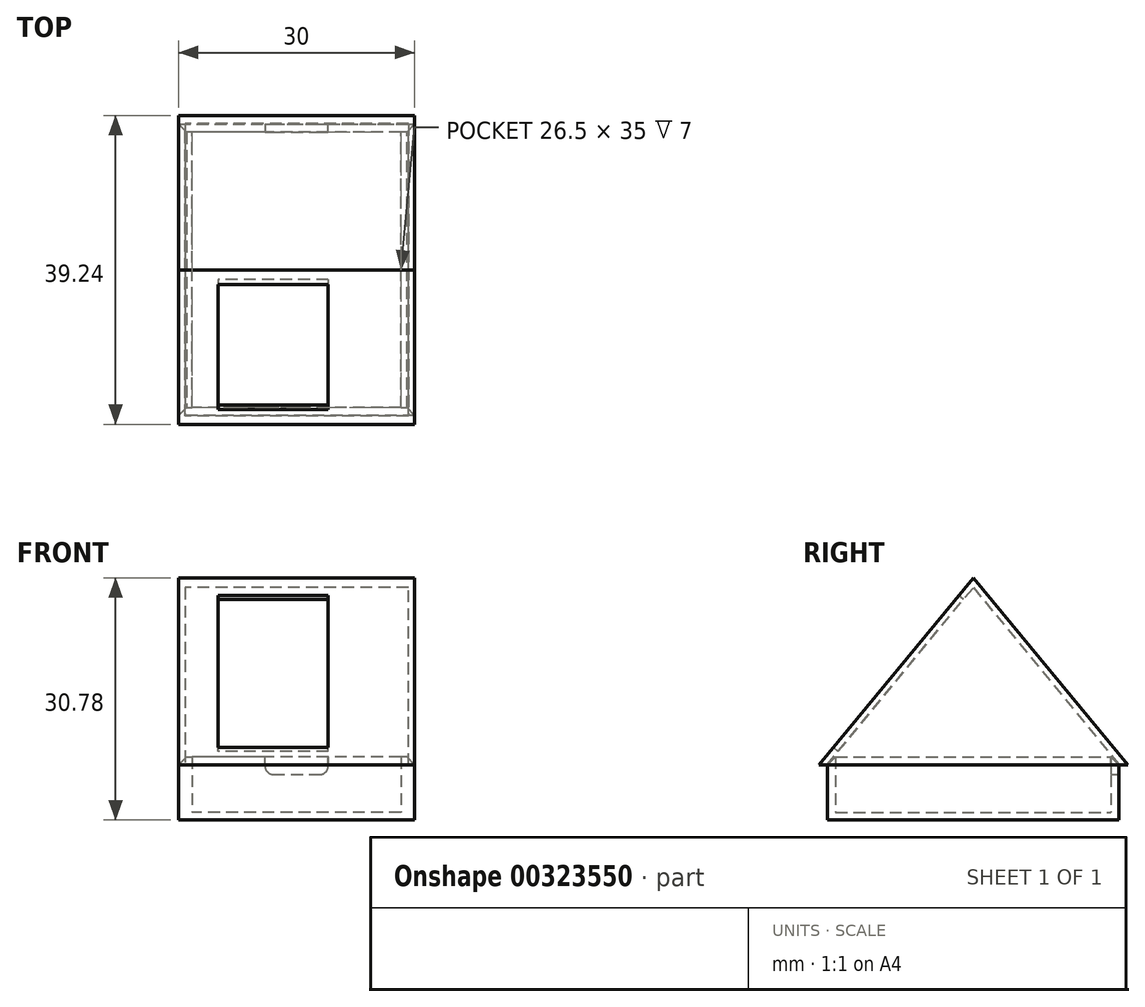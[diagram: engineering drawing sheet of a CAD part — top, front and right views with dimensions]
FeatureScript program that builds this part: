
annotation { "Feature Type Name" : "Feature", "Feature Type Description" : "" }
export const myFeature = defineFeature(function(context is Context, id is Id, definition is map)
    precondition{}
    {
        {
            var Q0;
            Q0=qCreatedBy(makeId("Top.planeOp"),FACE);
            var sketch = newSketch(context, id + "F0", { "sketchPlane" : qUnion([Q0])});
            skLineSegment(sketch, "E0.bottom", {"start": v(13.25, -17.5) * mm, "end": v(-13.25, -17.5) * mm});
            skLineSegment(sketch, "E0.top", {"start": v(13.25, 17.5) * mm, "end": v(-13.25, 17.5) * mm});
            skLineSegment(sketch, "E0.left", {"start": v(13.25, -17.5) * mm, "end": v(13.25, 17.5) * mm});
            skLineSegment(sketch, "E0.right", {"start": v(-13.25, -17.5) * mm, "end": v(-13.25, 17.5) * mm});
            skPoint(sketch, "E0.middle", {"position": v(0, 0) * mm});
            skLineSegment(sketch, "E1.bottom", {"start": v(-15, -18.5) * mm, "end": v(15, -18.5) * mm});
            skLineSegment(sketch, "E1.top", {"start": v(-15, 18.5) * mm, "end": v(15, 18.5) * mm});
            skLineSegment(sketch, "E1.left", {"start": v(-15, -18.5) * mm, "end": v(-15, 18.5) * mm});
            skLineSegment(sketch, "E1.right", {"start": v(15, -18.5) * mm, "end": v(15, 18.5) * mm});
            skSolve(sketch);
        }
        {
            var Q0;
            Q0=makeQuery(id+"F0.imprint","IMPRINT",FACE,{"disambiguationData":[TD([[makeQuery(id+"F0.imprint","IMPRINT",EDGE,{"derivedFrom":sQuery(id+"F0.wireOp",EDGE,"E0.bottom")}),-1.0]])]});
            var Q1;
            Q1=makeQuery(id+"F0.imprint","IMPRINT",FACE,{"disambiguationData":[TD([[makeQuery(id+"F0.imprint","IMPRINT",EDGE,{"derivedFrom":sQuery(id+"F0.wireOp",EDGE,"E0.bottom")}),1.0]])]});
            extrude(context, id + "F1", {"entities" : qUnion([Q0, Q1]), "oppositeDirection" : true, "depth" : 1 * mm});
        }
        {
            var Q0;
            Q0=makeQuery(id+"F0.imprint","IMPRINT",FACE,{"disambiguationData":[TD([[makeQuery(id+"F0.imprint","IMPRINT",EDGE,{"derivedFrom":sQuery(id+"F0.wireOp",EDGE,"E0.bottom")}),1.0]])]});
            extrude(context, id + "F2", {"entities" : qUnion([Q0]), "operationType" : NewBodyOperationType.ADD, "depth" : 7 * mm});
        }
        {
            var Q0;
            {var subQ0=sQuery(id+"F0.wireOp",EDGE,"E1.top");Q0=makeQuery(id+"F2.boolean.opBoolean","MERGE",FACE,{"derivedFrom":[makeQuery(id+"F1.opExtrude","SWEPT_FACE",FACE,{"disambiguationData":[OSD([subQ0])]}),makeQuery(id+"F2.opExtrude","SWEPT_FACE",FACE,{"disambiguationData":[OSD([subQ0])]})]});}
            var sketch = newSketch(context, id + "F3", { "sketchPlane" : qUnion([Q0])});
            skLineSegment(sketch, "E2.bottom", {"start": v(4, 4.8) * mm, "end": v(-4, 4.8) * mm});
            skLineSegment(sketch, "E2.top", {"start": v(4, 9.2) * mm, "end": v(-4, 9.2) * mm});
            skLineSegment(sketch, "E2.left", {"start": v(4, 4.8) * mm, "end": v(4, 9.2) * mm});
            skLineSegment(sketch, "E2.right", {"start": v(-4, 4.8) * mm, "end": v(-4, 9.2) * mm});
            skPoint(sketch, "E2.middle", {"position": v(0, 7) * mm});
            skSolve(sketch);
        }
        {
            var Q0;
            {var subQ0=sQuery(id+"F3.wireOp",EDGE,"E2.bottom");Q0=makeQuery(id+"F3.imprint","IMPRINT",FACE,{"disambiguationData":[TD([[makeQuery(id+"F3.imprint","IMPRINT",EDGE,{"derivedFrom":subQ0}),-1.0]])]});}
            extrude(context, id + "F4", {"entities" : qUnion([Q0]), "operationType" : NewBodyOperationType.REMOVE, "endBound" : BoundingType.UP_TO_NEXT, "oppositeDirection" : true, "depth" : 25 * mm});
        }
        {
            var Q0;
            Q0=makeQuery(id+"F4.boolean.opBoolean","COPY",EDGE,{"derivedFrom":makeQuery(id+"F4.opExtrude","SWEPT_EDGE",EDGE,{"disambiguationData":[OSD([sQuery(id+"F3.wireOp",EDGE,"E2.bottom"),sQuery(id+"F3.wireOp",EDGE,"E2.left")])]})});
            var Q1;
            Q1=makeQuery(id+"F4.boolean.opBoolean","COPY",EDGE,{"derivedFrom":makeQuery(id+"F4.opExtrude","SWEPT_EDGE",EDGE,{"disambiguationData":[OSD([sQuery(id+"F3.wireOp",EDGE,"E2.bottom"),sQuery(id+"F3.wireOp",EDGE,"E2.right")])]})});
            fillet(context, id + "F5", {"entities" : qUnion([Q0, Q1]), "radius" : 1 * mm, "tangentPropagation" : true, "allowEdgeOverflow" : false});
        }
        {
            var Q0;
            Q0=makeQuery(id+"F2.opExtrude","CAP_EDGE",EDGE,{"disambiguationData":[OSD([sQuery(id+"F0.wireOp",EDGE,"E1.right")])],"isStart":false});
            var Q1;
            Q1=makeQuery(id+"F2.opExtrude","CAP_EDGE",EDGE,{"disambiguationData":[OSD([sQuery(id+"F0.wireOp",EDGE,"E1.bottom")])],"isStart":false});
            var Q2;
            Q2=makeQuery(id+"F2.opExtrude","CAP_EDGE",EDGE,{"disambiguationData":[OSD([sQuery(id+"F0.wireOp",EDGE,"E1.left")])],"isStart":false});
            var Q3;
            {var subQ0=sQuery(id+"F0.wireOp",EDGE,"E1.left");var subQ1=sQuery(id+"F0.wireOp",EDGE,"E1.top");Q3=makeQuery(id+"F4.boolean.opBoolean","SPLIT",EDGE,{"disambiguationData":[TD([makeQuery(id+"F1.opExtrude","SWEPT_FACE",FACE,{"disambiguationData":[OSD([subQ0])]})])],"derivedFrom":makeQuery(id+"F2.opExtrude","CAP_EDGE",EDGE,{"disambiguationData":[OSD([subQ1])],"isStart":false})});}
            var Q4;
            {var subQ0=sQuery(id+"F0.wireOp",EDGE,"E1.right");var subQ1=sQuery(id+"F0.wireOp",EDGE,"E1.top");Q4=makeQuery(id+"F4.boolean.opBoolean","SPLIT",EDGE,{"disambiguationData":[TD([makeQuery(id+"F1.opExtrude","SWEPT_FACE",FACE,{"disambiguationData":[OSD([subQ0])]})])],"derivedFrom":makeQuery(id+"F2.opExtrude","CAP_EDGE",EDGE,{"disambiguationData":[OSD([subQ1])],"isStart":false})});}
            chamfer(context, id + "F6", {"entities" : qUnion([Q0, Q1, Q2, Q3, Q4]), "width" : 1 * mm, "tangentPropagation" : true});
        }
        {
            var Q0;
            Q0=qCreatedBy(makeId("Right.planeOp"),FACE);
            var sketch = newSketch(context, id + "F7", { "sketchPlane" : qUnion([Q0])});
            skLineSegment(sketch, "E3", {"start": v(-17.5, 7) * mm, "end": v(0, 28.21) * mm});
            skLineSegment(sketch, "E4", {"start": v(0, 28.21) * mm, "end": v(17.5, 7) * mm});
            skLineSegment(sketch, "E5", {"start": v(17.5, 7) * mm, "end": v(-17.5, 7) * mm});
            skLineSegment(sketch, "E6.0", {"start": v(-19.62, 6) * mm, "end": v(0, 29.78) * mm});
            skLineSegment(sketch, "E6.1", {"start": v(19.62, 6) * mm, "end": v(-19.62, 6) * mm});
            skLineSegment(sketch, "E6.2", {"start": v(0, 29.78) * mm, "end": v(19.62, 6) * mm});
            skSolve(sketch);
        }
        {
            var Q0;
            Q0=makeQuery(id+"F7.imprint","IMPRINT",FACE,{"disambiguationData":[TD([[makeQuery(id+"F7.imprint","IMPRINT",EDGE,{"derivedFrom":sQuery(id+"F7.wireOp",EDGE,"E3")}),1.0]])]});
            var Q1;
            Q1=makeQuery(id+"F7.imprint","IMPRINT",FACE,{"disambiguationData":[TD([[makeQuery(id+"F7.imprint","IMPRINT",EDGE,{"derivedFrom":sQuery(id+"F7.wireOp",EDGE,"E3")}),-1.0]])]});
            var Q2;
            {var subQ0=sQuery(id+"F0.wireOp",EDGE,"E1.right");Q2=makeQuery(id+"F2.boolean.opBoolean","MERGE",FACE,{"derivedFrom":[makeQuery(id+"F1.opExtrude","SWEPT_FACE",FACE,{"disambiguationData":[OSD([subQ0])]}),makeQuery(id+"F2.opExtrude","SWEPT_FACE",FACE,{"disambiguationData":[OSD([subQ0])]})]});}
            var Q3;
            {var subQ0=sQuery(id+"F0.wireOp",EDGE,"E1.right");var subQ1=sQuery(id+"F0.wireOp",EDGE,"E1.bottom");Q3=makeQuery(id+"F6.opChamfer","BLEND_VERTEX",VERTEX,{"blendedFrom":[makeQuery(id+"F2.opExtrude","CAP_EDGE",EDGE,{"disambiguationData":[OSD([subQ1])],"isStart":false}),makeQuery(id+"F2.opExtrude","CAP_EDGE",EDGE,{"disambiguationData":[OSD([subQ0])],"isStart":false}),makeQuery(id+"F2.boolean.opBoolean","MERGE",FACE,{"derivedFrom":[makeQuery(id+"F1.opExtrude","SWEPT_FACE",FACE,{"disambiguationData":[OSD([subQ1])]}),makeQuery(id+"F2.opExtrude","SWEPT_FACE",FACE,{"disambiguationData":[OSD([subQ1])]})]}),makeQuery(id+"F2.boolean.opBoolean","MERGE",FACE,{"derivedFrom":[makeQuery(id+"F1.opExtrude","SWEPT_FACE",FACE,{"disambiguationData":[OSD([subQ0])]}),makeQuery(id+"F2.opExtrude","SWEPT_FACE",FACE,{"disambiguationData":[OSD([subQ0])]})]})],"blendedInto":[makeQuery(id+"F2.boolean.opBoolean","MERGE",FACE,{"derivedFrom":[makeQuery(id+"F1.opExtrude","SWEPT_FACE",FACE,{"disambiguationData":[OSD([subQ1])]}),makeQuery(id+"F2.opExtrude","SWEPT_FACE",FACE,{"disambiguationData":[OSD([subQ1])]})]}),makeQuery(id+"F2.boolean.opBoolean","MERGE",FACE,{"derivedFrom":[makeQuery(id+"F1.opExtrude","SWEPT_FACE",FACE,{"disambiguationData":[OSD([subQ0])]}),makeQuery(id+"F2.opExtrude","SWEPT_FACE",FACE,{"disambiguationData":[OSD([subQ0])]})]})]});}
            var Q4;
            {var subQ0=sQuery(id+"F0.wireOp",EDGE,"E1.left");var subQ1=sQuery(id+"F0.wireOp",EDGE,"E1.bottom");Q4=makeQuery(id+"F6.opChamfer","BLEND_VERTEX",VERTEX,{"blendedFrom":[makeQuery(id+"F2.opExtrude","CAP_EDGE",EDGE,{"disambiguationData":[OSD([subQ1])],"isStart":false}),makeQuery(id+"F2.opExtrude","CAP_EDGE",EDGE,{"disambiguationData":[OSD([subQ0])],"isStart":false}),makeQuery(id+"F2.boolean.opBoolean","MERGE",FACE,{"derivedFrom":[makeQuery(id+"F1.opExtrude","SWEPT_FACE",FACE,{"disambiguationData":[OSD([subQ1])]}),makeQuery(id+"F2.opExtrude","SWEPT_FACE",FACE,{"disambiguationData":[OSD([subQ1])]})]}),makeQuery(id+"F2.boolean.opBoolean","MERGE",FACE,{"derivedFrom":[makeQuery(id+"F1.opExtrude","SWEPT_FACE",FACE,{"disambiguationData":[OSD([subQ0])]}),makeQuery(id+"F2.opExtrude","SWEPT_FACE",FACE,{"disambiguationData":[OSD([subQ0])]})]})],"blendedInto":[makeQuery(id+"F2.boolean.opBoolean","MERGE",FACE,{"derivedFrom":[makeQuery(id+"F1.opExtrude","SWEPT_FACE",FACE,{"disambiguationData":[OSD([subQ1])]}),makeQuery(id+"F2.opExtrude","SWEPT_FACE",FACE,{"disambiguationData":[OSD([subQ1])]})]}),makeQuery(id+"F2.boolean.opBoolean","MERGE",FACE,{"derivedFrom":[makeQuery(id+"F1.opExtrude","SWEPT_FACE",FACE,{"disambiguationData":[OSD([subQ0])]}),makeQuery(id+"F2.opExtrude","SWEPT_FACE",FACE,{"disambiguationData":[OSD([subQ0])]})]})]});}
            extrude(context, id + "F8", {"entities" : qUnion([Q0, Q1]), "endBound" : BoundingType.UP_TO_VERTEX, "endBoundEntityFace" : qUnion([Q2]), "endBoundEntityVertex" : qUnion([Q3]), "depth" : 25 * mm, "hasSecondDirection" : true, "secondDirectionBound" : SecondDirectionBoundingType.UP_TO_VERTEX, "secondDirectionOppositeDirection" : true, "secondDirectionBoundEntityVertex" : qUnion([Q4]), "secondDirectionDepth" : 25 * mm});
        }
        {
            var Q0;
            Q0=makeQuery(id+"F8.opExtrude","SWEPT_FACE",FACE,{"disambiguationData":[OSD([sQuery(id+"F7.wireOp",EDGE,"E6.1")])]});
            shell(context, id + "F9", {"entities" : qUnion([Q0]), "thickness" : 0.8 * mm});
        }
        {
            var Q0;
            Q0=makeQuery(id+"F8.opExtrude","SWEPT_FACE",FACE,{"disambiguationData":[OSD([sQuery(id+"F7.wireOp",EDGE,"E6.0")])]});
            var sketch = newSketch(context, id + "F10", { "sketchPlane" : qUnion([Q0])});
            skLineSegment(sketch, "E7.bottom", {"start": v(-10, 20.06) * mm, "end": v(4, 20.06) * mm});
            skLineSegment(sketch, "E7.top", {"start": v(-10, -4.94) * mm, "end": v(4, -4.94) * mm});
            skLineSegment(sketch, "E7.left", {"start": v(-10, 20.06) * mm, "end": v(-10, -4.94) * mm});
            skLineSegment(sketch, "E7.right", {"start": v(4, 20.06) * mm, "end": v(4, -4.94) * mm});
            skLineSegment(sketch, "E8", {"start": v(-3, 20.06) * mm, "end": v(-3, 22.98) * mm, "construction": true});
            skLineSegment(sketch, "E9", {"start": v(-3, -4.94) * mm, "end": v(-3, -7.86) * mm, "construction": true});
            skSolve(sketch);
        }
        {
            var Q0;
            Q0=makeQuery(id+"F10.imprint","IMPRINT",FACE,{"disambiguationData":[TD([[makeQuery(id+"F10.imprint","IMPRINT",EDGE,{"derivedFrom":sQuery(id+"F10.wireOp",EDGE,"E7.bottom")}),-1.0]])]});
            extrude(context, id + "F11", {"entities" : qUnion([Q0]), "operationType" : NewBodyOperationType.REMOVE, "endBound" : BoundingType.UP_TO_NEXT, "oppositeDirection" : true, "depth" : 25 * mm});
        }
    });
